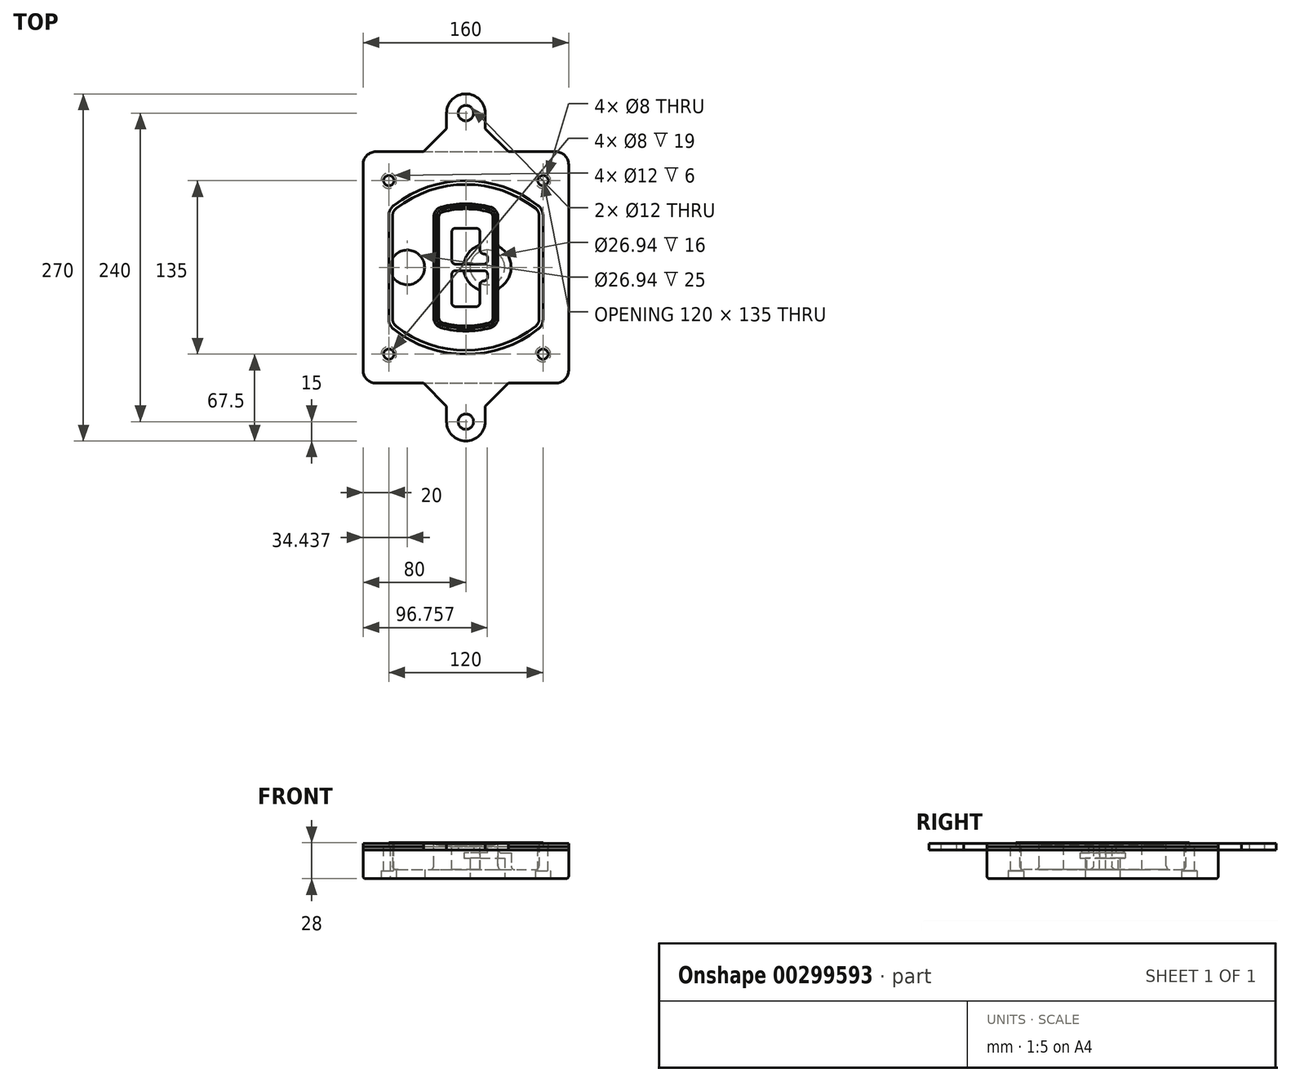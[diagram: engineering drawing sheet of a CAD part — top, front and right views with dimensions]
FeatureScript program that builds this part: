
annotation { "Feature Type Name" : "Feature", "Feature Type Description" : "" }
export const myFeature = defineFeature(function(context is Context, id is Id, definition is map)
    precondition{}
    {
        {
            var Q0;
            Q0=qCreatedBy(makeId("Top.planeOp"),FACE);
            var sketch = newSketch(context, id + "F0", { "sketchPlane" : qUnion([Q0])});
            skPoint(sketch, "E0.rect.middle", {"position": v(0, 0) * mm});
            skLineSegment(sketch, "E1.bottom", {"start": v(-70, -90) * mm, "end": v(70, -90) * mm});
            skLineSegment(sketch, "E1.top", {"start": v(-70, 90) * mm, "end": v(70, 90) * mm});
            skLineSegment(sketch, "E1.left", {"start": v(-80, -80) * mm, "end": v(-80, 80) * mm});
            skLineSegment(sketch, "E1.right", {"start": v(80, -80) * mm, "end": v(80, 80) * mm});
            skLineSegment(sketch, "E2", {"start": v(-80, 90) * mm, "end": v(80, -90) * mm, "construction": true});
            skLineSegment(sketch, "E3", {"start": v(80, 90) * mm, "end": v(-80, -90) * mm, "construction": true});
            skCircle(sketch, "E4", {"center": v(-60, 67.5) * mm, "radius": 4 * mm});
            skCircle(sketch, "E5", {"center": v(60, 67.5) * mm, "radius": 4 * mm});
            skCircle(sketch, "E6", {"center": v(60, -67.5) * mm, "radius": 4 * mm});
            skCircle(sketch, "E7", {"center": v(-60, -67.5) * mm, "radius": 4 * mm});
            skLineSegment(sketch, "E8", {"start": v(-60, 67.5) * mm, "end": v(60, 67.5) * mm, "construction": true});
            skLineSegment(sketch, "E9", {"start": v(60, 67.5) * mm, "end": v(60, -67.5) * mm, "construction": true});
            skLineSegment(sketch, "E10", {"start": v(60, -67.5) * mm, "end": v(-60, -67.5) * mm, "construction": true});
            skLineSegment(sketch, "E11", {"start": v(-60, -67.5) * mm, "end": v(-60, 67.5) * mm, "construction": true});
            skLineSegment(sketch, "E12", {"start": v(-60, 40.3) * mm, "end": v(-60, -40.3) * mm});
            skLineSegment(sketch, "E13", {"start": v(60, 40.3) * mm, "end": v(60, -40.3) * mm});
            skArc(sketch, "E14", {"start": v(56.15, 48.18) * mm, "mid": v(0, 67.5) * mm, "end": v(-56.15, 48.18) * mm});
            skArc(sketch, "E15", {"start": v(-56.15, -48.18) * mm, "mid": v(0, -67.5) * mm, "end": v(56.15, -48.18) * mm});
            skLineSegment(sketch, "E16", {"start": v(-60, 0) * mm, "end": v(60, 0) * mm, "construction": true});
            skPoint(sketch, "E17.visualSharp", {"position": v(-60, -45) * mm});
            skArc(sketch, "E17.filletArc", {"start": v(-60, -40.3) * mm, "mid": v(-58.99, -44.68) * mm, "end": v(-56.15, -48.18) * mm});
            skPoint(sketch, "E18.visualSharp", {"position": v(-60, 45) * mm});
            skArc(sketch, "E18.filletArc", {"start": v(-56.15, 48.18) * mm, "mid": v(-58.99, 44.68) * mm, "end": v(-60, 40.3) * mm});
            skPoint(sketch, "E19.visualSharp", {"position": v(60, 45) * mm});
            skArc(sketch, "E19.filletArc", {"start": v(60, 40.3) * mm, "mid": v(58.99, 44.68) * mm, "end": v(56.15, 48.18) * mm});
            skPoint(sketch, "E20.visualSharp", {"position": v(60, -45) * mm});
            skArc(sketch, "E20.filletArc", {"start": v(56.15, -48.18) * mm, "mid": v(58.99, -44.68) * mm, "end": v(60, -40.3) * mm});
            skPoint(sketch, "E21.visualSharp", {"position": v(-80, 90) * mm});
            skArc(sketch, "E21.filletArc", {"start": v(-70, 90) * mm, "mid": v(-77.07, 87.07) * mm, "end": v(-80, 80) * mm});
            skPoint(sketch, "E22.visualSharp", {"position": v(80, 90) * mm});
            skArc(sketch, "E22.filletArc", {"start": v(80, 80) * mm, "mid": v(77.07, 87.07) * mm, "end": v(70, 90) * mm});
            skPoint(sketch, "E23.visualSharp", {"position": v(80, -90) * mm});
            skArc(sketch, "E23.filletArc", {"start": v(70, -90) * mm, "mid": v(77.07, -87.07) * mm, "end": v(80, -80) * mm});
            skPoint(sketch, "E24.visualSharp", {"position": v(-80, -90) * mm});
            skArc(sketch, "E24.filletArc", {"start": v(-80, -80) * mm, "mid": v(-77.07, -87.07) * mm, "end": v(-70, -90) * mm});
            skArc(sketch, "E25.0", {"start": v(57, 40.3) * mm, "mid": v(56.3, 43.36) * mm, "end": v(54.3, 45.81) * mm});
            skLineSegment(sketch, "E25.1", {"start": v(57, 40.3) * mm, "end": v(57, -40.3) * mm});
            skArc(sketch, "E25.2", {"start": v(54.3, -45.81) * mm, "mid": v(56.3, -43.36) * mm, "end": v(57, -40.3) * mm});
            skArc(sketch, "E25.3", {"start": v(-54.3, -45.81) * mm, "mid": v(0, -64.5) * mm, "end": v(54.3, -45.81) * mm});
            skArc(sketch, "E25.4", {"start": v(-57, -40.3) * mm, "mid": v(-56.3, -43.36) * mm, "end": v(-54.3, -45.81) * mm});
            skArc(sketch, "E25.5", {"start": v(54.3, 45.81) * mm, "mid": v(0, 64.5) * mm, "end": v(-54.3, 45.81) * mm});
            skLineSegment(sketch, "E25.6", {"start": v(-57, 40.3) * mm, "end": v(-57, -40.3) * mm});
            skArc(sketch, "E25.7", {"start": v(-54.3, 45.81) * mm, "mid": v(-56.3, 43.36) * mm, "end": v(-57, 40.3) * mm});
            skArc(sketch, "E26.0", {"start": v(-58.62, 51.33) * mm, "mid": v(-62.58, 46.43) * mm, "end": v(-64, 40.3) * mm});
            skArc(sketch, "E26.1", {"start": v(58.62, 51.33) * mm, "mid": v(0, 71.5) * mm, "end": v(-58.62, 51.33) * mm});
            skArc(sketch, "E26.2", {"start": v(64, 40.3) * mm, "mid": v(62.58, 46.43) * mm, "end": v(58.62, 51.33) * mm});
            skLineSegment(sketch, "E26.3", {"start": v(64, 40.3) * mm, "end": v(64, -40.3) * mm});
            skArc(sketch, "E26.4", {"start": v(58.62, -51.33) * mm, "mid": v(62.58, -46.43) * mm, "end": v(64, -40.3) * mm});
            skLineSegment(sketch, "E26.5", {"start": v(-64, 40.3) * mm, "end": v(-64, -40.3) * mm});
            skArc(sketch, "E26.6", {"start": v(-58.62, -51.33) * mm, "mid": v(0, -71.5) * mm, "end": v(58.62, -51.33) * mm});
            skArc(sketch, "E26.7", {"start": v(-64, -40.3) * mm, "mid": v(-62.58, -46.43) * mm, "end": v(-58.62, -51.33) * mm});
            skSolve(sketch);
        }
        {
            var Q0;
            Q0=makeQuery(id+"F0.imprint","IMPRINT",FACE,{"disambiguationData":[TD([[makeQuery(id+"F0.imprint","IMPRINT",EDGE,{"derivedFrom":sQuery(id+"F0.wireOp",EDGE,"E1.bottom")}),1.0]])]});
            var Q1;
            Q1=makeQuery(id+"F0.imprint","IMPRINT",FACE,{"disambiguationData":[TD([[makeQuery(id+"F0.imprint","IMPRINT",EDGE,{"derivedFrom":sQuery(id+"F0.wireOp",EDGE,"E12")}),1.0]])]});
            var Q2;
            Q2=makeQuery(id+"F0.imprint","IMPRINT",FACE,{"disambiguationData":[TD([[makeQuery(id+"F0.imprint","IMPRINT",EDGE,{"derivedFrom":sQuery(id+"F0.wireOp",EDGE,"E25.0")}),1.0]])]});
            var Q3;
            Q3=makeQuery(id+"F0.imprint","IMPRINT",FACE,{"disambiguationData":[TD([[makeQuery(id+"F0.imprint","IMPRINT",EDGE,{"derivedFrom":sQuery(id+"F0.wireOp",EDGE,"E12")}),-1.0]])]});
            extrude(context, id + "F1", {"entities" : qUnion([Q0, Q1, Q2, Q3]), "oppositeDirection" : true, "depth" : 25 * mm});
        }
        {
            var Q0;
            Q0=makeQuery(id+"F0.imprint","IMPRINT",FACE,{"disambiguationData":[TD([[makeQuery(id+"F0.imprint","IMPRINT",EDGE,{"derivedFrom":sQuery(id+"F0.wireOp",EDGE,"E12")}),1.0]])]});
            extrude(context, id + "F2", {"entities" : qUnion([Q0]), "operationType" : NewBodyOperationType.ADD, "depth" : 3 * mm});
        }
        {
            var Q0;
            Q0=makeQuery(id+"F0.imprint","IMPRINT",FACE,{"disambiguationData":[TD([[makeQuery(id+"F0.imprint","IMPRINT",EDGE,{"derivedFrom":sQuery(id+"F0.wireOp",EDGE,"E25.0")}),1.0]])]});
            extrude(context, id + "F3", {"entities" : qUnion([Q0]), "operationType" : NewBodyOperationType.REMOVE, "oppositeDirection" : true, "depth" : 18 * mm});
        }
        {
            var Q0;
            Q0=makeQuery(id+"F2.opExtrude","CAP_FACE",FACE,{"disambiguationData":[OSD([sQuery(id+"F0.wireOp",EDGE,"E12"),sQuery(id+"F0.wireOp",EDGE,"E13"),sQuery(id+"F0.wireOp",EDGE,"E14"),sQuery(id+"F0.wireOp",EDGE,"E15"),sQuery(id+"F0.wireOp",EDGE,"E17.filletArc"),sQuery(id+"F0.wireOp",EDGE,"E18.filletArc"),sQuery(id+"F0.wireOp",EDGE,"E19.filletArc"),sQuery(id+"F0.wireOp",EDGE,"E20.filletArc"),sQuery(id+"F0.wireOp",EDGE,"E25.0"),sQuery(id+"F0.wireOp",EDGE,"E25.1"),sQuery(id+"F0.wireOp",EDGE,"E25.2"),sQuery(id+"F0.wireOp",EDGE,"E25.3"),sQuery(id+"F0.wireOp",EDGE,"E25.4"),sQuery(id+"F0.wireOp",EDGE,"E25.5"),sQuery(id+"F0.wireOp",EDGE,"E25.6"),sQuery(id+"F0.wireOp",EDGE,"E25.7")])],"isStart":false});
            var sketch = newSketch(context, id + "F4", { "sketchPlane" : qUnion([Q0])});
            skArc(sketch, "E27.0", {"start": v(-19.08, -46.97) * mm, "mid": v(0, -49.5) * mm, "end": v(19.08, -46.97) * mm});
            skArc(sketch, "E28.0", {"start": v(19.08, 46.97) * mm, "mid": v(0, 49.5) * mm, "end": v(-19.08, 46.97) * mm});
            skLineSegment(sketch, "E29", {"start": v(-25, 39.25) * mm, "end": v(-25, -39.25) * mm});
            skLineSegment(sketch, "E30", {"start": v(25, 39.25) * mm, "end": v(25, -39.25) * mm});
            skLineSegment(sketch, "E31", {"start": v(-25, 45.1) * mm, "end": v(25, 45.1) * mm, "construction": true});
            skLineSegment(sketch, "E32", {"start": v(-25, -45.1) * mm, "end": v(25, -45.1) * mm, "construction": true});
            skPoint(sketch, "E33.visualSharp", {"position": v(-25, 45.1) * mm});
            skArc(sketch, "E33.filletArc", {"start": v(-19.08, 46.97) * mm, "mid": v(-23.35, 44.11) * mm, "end": v(-25, 39.25) * mm});
            skPoint(sketch, "E34.visualSharp", {"position": v(25, 45.1) * mm});
            skArc(sketch, "E34.filletArc", {"start": v(25, 39.25) * mm, "mid": v(23.35, 44.11) * mm, "end": v(19.08, 46.97) * mm});
            skPoint(sketch, "E35.visualSharp", {"position": v(25, -45.1) * mm});
            skArc(sketch, "E35.filletArc", {"start": v(19.08, -46.97) * mm, "mid": v(23.35, -44.11) * mm, "end": v(25, -39.25) * mm});
            skPoint(sketch, "E36.visualSharp", {"position": v(-25, -45.1) * mm});
            skArc(sketch, "E36.filletArc", {"start": v(-25, -39.25) * mm, "mid": v(-23.35, -44.11) * mm, "end": v(-19.08, -46.97) * mm});
            skArc(sketch, "E37.0", {"start": v(54.3, 45.81) * mm, "mid": v(0, 64.5) * mm, "end": v(-54.3, 45.81) * mm});
            skArc(sketch, "E37.1", {"start": v(-54.3, 45.81) * mm, "mid": v(-56.3, 43.36) * mm, "end": v(-57, 40.3) * mm});
            skLineSegment(sketch, "E37.2", {"start": v(-57, 40.3) * mm, "end": v(-57, -40.3) * mm});
            skArc(sketch, "E37.3", {"start": v(-57, -40.3) * mm, "mid": v(-56.3, -43.36) * mm, "end": v(-54.3, -45.81) * mm});
            skArc(sketch, "E37.4", {"start": v(-54.3, -45.81) * mm, "mid": v(0, -64.5) * mm, "end": v(54.3, -45.81) * mm});
            skArc(sketch, "E37.5", {"start": v(54.3, -45.81) * mm, "mid": v(56.3, -43.36) * mm, "end": v(57, -40.3) * mm});
            skLineSegment(sketch, "E37.6", {"start": v(57, 40.3) * mm, "end": v(57, -40.3) * mm});
            skArc(sketch, "E37.7", {"start": v(57, 40.3) * mm, "mid": v(56.3, 43.36) * mm, "end": v(54.3, 45.81) * mm});
            skLineSegment(sketch, "E38.0", {"start": v(23, 39.25) * mm, "end": v(23, -39.25) * mm});
            skArc(sketch, "E38.1", {"start": v(18.56, -45.04) * mm, "mid": v(21.76, -42.9) * mm, "end": v(23, -39.25) * mm});
            skArc(sketch, "E38.2", {"start": v(-18.56, -45.04) * mm, "mid": v(0, -47.5) * mm, "end": v(18.56, -45.04) * mm});
            skArc(sketch, "E38.3", {"start": v(-23, -39.25) * mm, "mid": v(-21.76, -42.9) * mm, "end": v(-18.56, -45.04) * mm});
            skLineSegment(sketch, "E38.4", {"start": v(-23, 39.25) * mm, "end": v(-23, -39.25) * mm});
            skArc(sketch, "E38.5", {"start": v(23, 39.25) * mm, "mid": v(21.76, 42.9) * mm, "end": v(18.56, 45.04) * mm});
            skArc(sketch, "E38.6", {"start": v(-18.56, 45.04) * mm, "mid": v(-21.76, 42.9) * mm, "end": v(-23, 39.25) * mm});
            skArc(sketch, "E38.7", {"start": v(18.56, 45.04) * mm, "mid": v(0, 47.5) * mm, "end": v(-18.56, 45.04) * mm});
            skArc(sketch, "E39.0", {"start": v(21, 39.25) * mm, "mid": v(20.18, 41.68) * mm, "end": v(18.04, 43.1) * mm});
            skLineSegment(sketch, "E39.1", {"start": v(21, 39.25) * mm, "end": v(21, -39.25) * mm});
            skArc(sketch, "E39.2", {"start": v(18.04, -43.1) * mm, "mid": v(20.18, -41.68) * mm, "end": v(21, -39.25) * mm});
            skArc(sketch, "E39.3", {"start": v(-18.04, -43.1) * mm, "mid": v(0, -45.5) * mm, "end": v(18.04, -43.1) * mm});
            skArc(sketch, "E39.4", {"start": v(-21, -39.25) * mm, "mid": v(-20.18, -41.68) * mm, "end": v(-18.04, -43.1) * mm});
            skArc(sketch, "E39.5", {"start": v(18.04, 43.1) * mm, "mid": v(0, 45.5) * mm, "end": v(-18.04, 43.1) * mm});
            skLineSegment(sketch, "E39.6", {"start": v(-21, 39.25) * mm, "end": v(-21, -39.25) * mm});
            skArc(sketch, "E39.7", {"start": v(-18.04, 43.1) * mm, "mid": v(-20.18, 41.68) * mm, "end": v(-21, 39.25) * mm});
            skLineSegment(sketch, "E40", {"start": v(-25, 0) * mm, "end": v(25, 0) * mm, "construction": true});
            skLineSegment(sketch, "E41", {"start": v(-11, 5.5) * mm, "end": v(-11, 27.5) * mm});
            skLineSegment(sketch, "E42", {"start": v(-8, 30.5) * mm, "end": v(8, 30.5) * mm});
            skLineSegment(sketch, "E43", {"start": v(11, 27.5) * mm, "end": v(11, 13.5) * mm});
            skLineSegment(sketch, "E44", {"start": v(14, 10.5) * mm, "end": v(14, 10.5) * mm});
            skLineSegment(sketch, "E45", {"start": v(17, 7.5) * mm, "end": v(17, 5.5) * mm});
            skLineSegment(sketch, "E46", {"start": v(14, 2.5) * mm, "end": v(-8, 2.5) * mm});
            skPoint(sketch, "E47.visualSharp", {"position": v(-11, 30.5) * mm});
            skArc(sketch, "E47.filletArc", {"start": v(-8, 30.5) * mm, "mid": v(-10.12, 29.62) * mm, "end": v(-11, 27.5) * mm});
            skPoint(sketch, "E48.visualSharp", {"position": v(11, 30.5) * mm});
            skArc(sketch, "E48.filletArc", {"start": v(11, 27.5) * mm, "mid": v(10.12, 29.62) * mm, "end": v(8, 30.5) * mm});
            skPoint(sketch, "E49.visualSharp", {"position": v(11, 10.5) * mm});
            skArc(sketch, "E49.filletArc", {"start": v(11, 13.5) * mm, "mid": v(11.88, 11.38) * mm, "end": v(14, 10.5) * mm});
            skPoint(sketch, "E50.visualSharp", {"position": v(17, 10.5) * mm});
            skArc(sketch, "E50.filletArc", {"start": v(17, 7.5) * mm, "mid": v(16.12, 9.62) * mm, "end": v(14, 10.5) * mm});
            skPoint(sketch, "E51.visualSharp", {"position": v(17, 2.5) * mm});
            skArc(sketch, "E51.filletArc", {"start": v(14, 2.5) * mm, "mid": v(16.12, 3.38) * mm, "end": v(17, 5.5) * mm});
            skPoint(sketch, "E52.visualSharp", {"position": v(-11, 2.5) * mm});
            skArc(sketch, "E52.filletArc", {"start": v(-11, 5.5) * mm, "mid": v(-10.12, 3.38) * mm, "end": v(-8, 2.5) * mm});
            skLineSegment(sketch, "E53.0.MirrorCS", {"start": v(14, -2.5) * mm, "end": v(-8, -2.5) * mm});
            skArc(sketch, "E54.0.MirrorCS", {"start": v(-11, -5.5) * mm, "mid": v(-10.12, -3.38) * mm, "end": v(-8, -2.5) * mm});
            skLineSegment(sketch, "E55.0.MirrorCS", {"start": v(-11, -5.5) * mm, "end": v(-11, -27.5) * mm});
            skArc(sketch, "E56.0.MirrorCS", {"start": v(-8, -30.5) * mm, "mid": v(-10.12, -29.62) * mm, "end": v(-11, -27.5) * mm});
            skLineSegment(sketch, "E57.0.MirrorCS", {"start": v(-8, -30.5) * mm, "end": v(8, -30.5) * mm});
            skArc(sketch, "E58.0.MirrorCS", {"start": v(11, -27.5) * mm, "mid": v(10.12, -29.62) * mm, "end": v(8, -30.5) * mm});
            skLineSegment(sketch, "E59.0.MirrorCS", {"start": v(11, -27.5) * mm, "end": v(11, -13.5) * mm});
            skArc(sketch, "E60.0.MirrorCS", {"start": v(11, -13.5) * mm, "mid": v(11.88, -11.38) * mm, "end": v(14, -10.5) * mm});
            skArc(sketch, "E61.0.MirrorCS", {"start": v(17, -7.5) * mm, "mid": v(16.12, -9.62) * mm, "end": v(14, -10.5) * mm});
            skLineSegment(sketch, "E62.0.MirrorCS", {"start": v(17, -7.5) * mm, "end": v(17, -5.5) * mm});
            skArc(sketch, "E63.0.MirrorCS", {"start": v(14, -2.5) * mm, "mid": v(16.12, -3.38) * mm, "end": v(17, -5.5) * mm});
            skSolve(sketch);
        }
        {
            var Q0;
            Q0=makeQuery(id+"F4.imprint","IMPRINT",FACE,{"disambiguationData":[TD([[makeQuery(id+"F4.imprint","IMPRINT",EDGE,{"derivedFrom":sQuery(id+"F4.wireOp",EDGE,"E27.0")}),1.0]])]});
            var Q1;
            Q1=makeQuery(id+"F4.imprint","IMPRINT",FACE,{"disambiguationData":[TD([[makeQuery(id+"F4.imprint","IMPRINT",EDGE,{"derivedFrom":sQuery(id+"F4.wireOp",EDGE,"E38.0")}),-1.0]])]});
            var Q2;
            Q2=makeQuery(id+"F4.imprint","IMPRINT",FACE,{"disambiguationData":[TD([[makeQuery(id+"F4.imprint","IMPRINT",EDGE,{"derivedFrom":sQuery(id+"F4.wireOp",EDGE,"E39.0")}),1.0]])]});
            extrude(context, id + "F5", {"entities" : qUnion([Q0, Q1, Q2]), "operationType" : NewBodyOperationType.ADD, "endBound" : BoundingType.UP_TO_NEXT, "oppositeDirection" : true, "depth" : 25 * mm});
        }
        {
            var Q0;
            Q0=makeQuery(id+"F4.imprint","IMPRINT",FACE,{"disambiguationData":[TD([[makeQuery(id+"F4.imprint","IMPRINT",EDGE,{"derivedFrom":sQuery(id+"F4.wireOp",EDGE,"E38.0")}),-1.0]])]});
            extrude(context, id + "F6", {"entities" : qUnion([Q0]), "operationType" : NewBodyOperationType.REMOVE, "oppositeDirection" : true, "depth" : 2 * mm});
        }
        {
            var Q0;
            Q0=makeQuery(id+"F1.opExtrude","CAP_FACE",FACE,{"disambiguationData":[OSD([sQuery(id+"F0.wireOp",EDGE,"E1.bottom"),sQuery(id+"F0.wireOp",EDGE,"E1.top"),sQuery(id+"F0.wireOp",EDGE,"E1.left"),sQuery(id+"F0.wireOp",EDGE,"E1.right"),sQuery(id+"F0.wireOp",EDGE,"E4"),sQuery(id+"F0.wireOp",EDGE,"E5"),sQuery(id+"F0.wireOp",EDGE,"E6"),sQuery(id+"F0.wireOp",EDGE,"E7"),sQuery(id+"F0.wireOp",EDGE,"E21.filletArc"),sQuery(id+"F0.wireOp",EDGE,"E22.filletArc"),sQuery(id+"F0.wireOp",EDGE,"E23.filletArc"),sQuery(id+"F0.wireOp",EDGE,"E24.filletArc")])],"isStart":false});
            var sketch = newSketch(context, id + "F7", { "sketchPlane" : qUnion([Q0])});
            skCircle(sketch, "E64", {"center": v(16.76, 0) * mm, "radius": 13.47 * mm});
            skCircle(sketch, "E65", {"center": v(-45.56, 0) * mm, "radius": 13.47 * mm});
            skLineSegment(sketch, "E66", {"start": v(80, 0) * mm, "end": v(-80, 0) * mm});
            skCircle(sketch, "E67", {"center": v(16.76, 0) * mm, "radius": 18.47 * mm});
            skCircle(sketch, "E68", {"center": v(60, -67.5) * mm, "radius": 6 * mm});
            skCircle(sketch, "E69", {"center": v(-60, -67.5) * mm, "radius": 6 * mm});
            skCircle(sketch, "E70", {"center": v(-60, 67.5) * mm, "radius": 6 * mm});
            skCircle(sketch, "E71", {"center": v(60, 67.5) * mm, "radius": 6 * mm});
            skSolve(sketch);
        }
        {
            var Q0;
            {var subQ1=sQuery(id+"F7.wireOp",EDGE,"E66");var subQ4=sQuery(id+"F7.wireOp",EDGE,"E64");var subQ6=makeQuery(id+"F7.imprint","INTERSECT",VERTEX,{"disambiguationData":[OD(0.0)],"derivedFrom":[subQ4,subQ1]});Q0=makeQuery(id+"F7.imprint","IMPRINT",FACE,{"disambiguationData":[TD([[makeQuery(id+"F7.imprint","IMPRINT",EDGE,{"disambiguationData":[TD([[subQ6,-1.0]])],"derivedFrom":subQ4}),-1.0]])]});}
            var Q1;
            {var subQ0=sQuery(id+"F7.wireOp",EDGE,"E66");var subQ1=sQuery(id+"F7.wireOp",EDGE,"E64");var subQ3=makeQuery(id+"F7.imprint","INTERSECT",VERTEX,{"disambiguationData":[OD(0.0)],"derivedFrom":[subQ1,subQ0]});Q1=makeQuery(id+"F7.imprint","IMPRINT",FACE,{"disambiguationData":[TD([[makeQuery(id+"F7.imprint","IMPRINT",EDGE,{"disambiguationData":[TD([[subQ3,-1.0]])],"derivedFrom":subQ1}),1.0]])]});}
            var Q2;
            {var subQ0=sQuery(id+"F7.wireOp",EDGE,"E66");var subQ1=sQuery(id+"F7.wireOp",EDGE,"E64");var subQ3=makeQuery(id+"F7.imprint","INTERSECT",VERTEX,{"disambiguationData":[OD(0.0)],"derivedFrom":[subQ1,subQ0]});Q2=makeQuery(id+"F7.imprint","IMPRINT",FACE,{"disambiguationData":[TD([[makeQuery(id+"F7.imprint","IMPRINT",EDGE,{"disambiguationData":[TD([[subQ3,1.0]])],"derivedFrom":subQ1}),1.0]])]});}
            var Q3;
            {var subQ1=sQuery(id+"F7.wireOp",EDGE,"E66");var subQ4=sQuery(id+"F7.wireOp",EDGE,"E64");var subQ6=makeQuery(id+"F7.imprint","INTERSECT",VERTEX,{"disambiguationData":[OD(0.0)],"derivedFrom":[subQ4,subQ1]});Q3=makeQuery(id+"F7.imprint","IMPRINT",FACE,{"disambiguationData":[TD([[makeQuery(id+"F7.imprint","IMPRINT",EDGE,{"disambiguationData":[TD([[subQ6,1.0]])],"derivedFrom":subQ4}),-1.0]])]});}
            extrude(context, id + "F8", {"entities" : qUnion([Q0, Q1, Q2, Q3]), "operationType" : NewBodyOperationType.ADD, "oppositeDirection" : true, "depth" : 20 * mm});
        }
        {
            var Q0;
            {var subQ0=sQuery(id+"F7.wireOp",EDGE,"E66");var subQ1=sQuery(id+"F7.wireOp",EDGE,"E64");var subQ3=makeQuery(id+"F7.imprint","INTERSECT",VERTEX,{"disambiguationData":[OD(0.0)],"derivedFrom":[subQ1,subQ0]});Q0=makeQuery(id+"F7.imprint","IMPRINT",FACE,{"disambiguationData":[TD([[makeQuery(id+"F7.imprint","IMPRINT",EDGE,{"disambiguationData":[TD([[subQ3,-1.0]])],"derivedFrom":subQ1}),1.0]])]});}
            var Q1;
            {var subQ0=sQuery(id+"F7.wireOp",EDGE,"E66");var subQ1=sQuery(id+"F7.wireOp",EDGE,"E64");var subQ3=makeQuery(id+"F7.imprint","INTERSECT",VERTEX,{"disambiguationData":[OD(0.0)],"derivedFrom":[subQ1,subQ0]});Q1=makeQuery(id+"F7.imprint","IMPRINT",FACE,{"disambiguationData":[TD([[makeQuery(id+"F7.imprint","IMPRINT",EDGE,{"disambiguationData":[TD([[subQ3,1.0]])],"derivedFrom":subQ1}),1.0]])]});}
            extrude(context, id + "F9", {"entities" : qUnion([Q0, Q1]), "operationType" : NewBodyOperationType.REMOVE, "oppositeDirection" : true, "depth" : 16 * mm});
        }
        {
            var Q0;
            {var subQ0=sQuery(id+"F7.wireOp",EDGE,"E66");var subQ1=sQuery(id+"F7.wireOp",EDGE,"E65");var subQ3=makeQuery(id+"F7.imprint","INTERSECT",VERTEX,{"disambiguationData":[OD(0.0)],"derivedFrom":[subQ1,subQ0]});Q0=makeQuery(id+"F7.imprint","IMPRINT",FACE,{"disambiguationData":[TD([[makeQuery(id+"F7.imprint","IMPRINT",EDGE,{"disambiguationData":[TD([[subQ3,-1.0]])],"derivedFrom":subQ1}),1.0]])]});}
            var Q1;
            {var subQ0=sQuery(id+"F7.wireOp",EDGE,"E66");var subQ1=sQuery(id+"F7.wireOp",EDGE,"E65");var subQ3=makeQuery(id+"F7.imprint","INTERSECT",VERTEX,{"disambiguationData":[OD(0.0)],"derivedFrom":[subQ1,subQ0]});Q1=makeQuery(id+"F7.imprint","IMPRINT",FACE,{"disambiguationData":[TD([[makeQuery(id+"F7.imprint","IMPRINT",EDGE,{"disambiguationData":[TD([[subQ3,1.0]])],"derivedFrom":subQ1}),1.0]])]});}
            extrude(context, id + "F10", {"entities" : qUnion([Q0, Q1]), "operationType" : NewBodyOperationType.REMOVE, "oppositeDirection" : true, "depth" : 25 * mm});
        }
        {
            var Q0;
            Q0=makeQuery(id+"F7.imprint","IMPRINT",FACE,{"disambiguationData":[TD([[makeQuery(id+"F7.imprint","IMPRINT",EDGE,{"derivedFrom":sQuery(id+"F7.wireOp",EDGE,"E68")}),1.0]])]});
            var Q1;
            Q1=makeQuery(id+"F7.imprint","IMPRINT",FACE,{"disambiguationData":[TD([[makeQuery(id+"F7.imprint","IMPRINT",EDGE,{"derivedFrom":makeQuery(id+"F1.opExtrude","CAP_EDGE",EDGE,{"disambiguationData":[OSD([sQuery(id+"F0.wireOp",EDGE,"E5")])],"isStart":false})}),-1.0]])]});
            var Q2;
            Q2=makeQuery(id+"F7.imprint","IMPRINT",FACE,{"disambiguationData":[TD([[makeQuery(id+"F7.imprint","IMPRINT",EDGE,{"derivedFrom":sQuery(id+"F7.wireOp",EDGE,"E69")}),1.0]])]});
            var Q3;
            Q3=makeQuery(id+"F7.imprint","IMPRINT",FACE,{"disambiguationData":[TD([[makeQuery(id+"F7.imprint","IMPRINT",EDGE,{"derivedFrom":makeQuery(id+"F1.opExtrude","CAP_EDGE",EDGE,{"disambiguationData":[OSD([sQuery(id+"F0.wireOp",EDGE,"E4")])],"isStart":false})}),-1.0]])]});
            var Q4;
            Q4=makeQuery(id+"F7.imprint","IMPRINT",FACE,{"disambiguationData":[TD([[makeQuery(id+"F7.imprint","IMPRINT",EDGE,{"derivedFrom":sQuery(id+"F7.wireOp",EDGE,"E70")}),1.0]])]});
            var Q5;
            Q5=makeQuery(id+"F7.imprint","IMPRINT",FACE,{"disambiguationData":[TD([[makeQuery(id+"F7.imprint","IMPRINT",EDGE,{"derivedFrom":makeQuery(id+"F1.opExtrude","CAP_EDGE",EDGE,{"disambiguationData":[OSD([sQuery(id+"F0.wireOp",EDGE,"E7")])],"isStart":false})}),-1.0]])]});
            var Q6;
            Q6=makeQuery(id+"F7.imprint","IMPRINT",FACE,{"disambiguationData":[TD([[makeQuery(id+"F7.imprint","IMPRINT",EDGE,{"derivedFrom":sQuery(id+"F7.wireOp",EDGE,"E71")}),1.0]])]});
            var Q7;
            Q7=makeQuery(id+"F7.imprint","IMPRINT",FACE,{"disambiguationData":[TD([[makeQuery(id+"F7.imprint","IMPRINT",EDGE,{"derivedFrom":makeQuery(id+"F1.opExtrude","CAP_EDGE",EDGE,{"disambiguationData":[OSD([sQuery(id+"F0.wireOp",EDGE,"E6")])],"isStart":false})}),-1.0]])]});
            extrude(context, id + "F11", {"entities" : qUnion([Q0, Q1, Q2, Q3, Q4, Q5, Q6, Q7]), "operationType" : NewBodyOperationType.REMOVE, "oppositeDirection" : true, "depth" : 6 * mm});
        }
        {
            var Q0;
            Q0=makeQuery(id+"F9.boolean.opBoolean","COPY",FACE,{"derivedFrom":makeQuery(id+"F9.opExtrude","CAP_FACE",FACE,{"disambiguationData":[OSD([sQuery(id+"F7.wireOp",EDGE,"E64")])],"isStart":false})});
            var sketch = newSketch(context, id + "F12", { "sketchPlane" : qUnion([Q0])});
            skArc(sketch, "E72.0", {"start": v(11, 17.55) * mm, "mid": v(2.57, 11.82) * mm, "end": v(-1.54, 2.5) * mm});
            skArc(sketch, "E72.1", {"start": v(-1.54, -2.5) * mm, "mid": v(2.57, -11.82) * mm, "end": v(11, -17.55) * mm});
            skLineSegment(sketch, "E73", {"start": v(-1.54, -2.5) * mm, "end": v(14, -2.5) * mm});
            skLineSegment(sketch, "E74.0", {"start": v(14, 2.5) * mm, "end": v(-1.54, 2.5) * mm});
            skArc(sketch, "E74.1", {"start": v(14, 2.5) * mm, "mid": v(16.12, 3.38) * mm, "end": v(17, 5.5) * mm});
            skLineSegment(sketch, "E74.2", {"start": v(17, 7.5) * mm, "end": v(17, 5.5) * mm});
            skArc(sketch, "E74.3", {"start": v(17, 7.5) * mm, "mid": v(16.12, 9.62) * mm, "end": v(14, 10.5) * mm});
            skArc(sketch, "E74.4", {"start": v(11, 13.5) * mm, "mid": v(11.88, 11.38) * mm, "end": v(14, 10.5) * mm});
            skLineSegment(sketch, "E74.5", {"start": v(11, 17.55) * mm, "end": v(11, 13.5) * mm});
            skLineSegment(sketch, "E74.7", {"start": v(14, -2.5) * mm, "end": v(-1.54, -2.5) * mm});
            skArc(sketch, "E74.8", {"start": v(14, -2.5) * mm, "mid": v(16.12, -3.38) * mm, "end": v(17, -5.5) * mm});
            skLineSegment(sketch, "E74.9", {"start": v(17, -7.5) * mm, "end": v(17, -5.5) * mm});
            skArc(sketch, "E74.10", {"start": v(17, -7.5) * mm, "mid": v(16.12, -9.62) * mm, "end": v(14, -10.5) * mm});
            skArc(sketch, "E74.11", {"start": v(11, -13.5) * mm, "mid": v(11.88, -11.38) * mm, "end": v(14, -10.5) * mm});
            skLineSegment(sketch, "E74.12", {"start": v(11, -17.55) * mm, "end": v(11, -13.5) * mm});
            skPoint(sketch, "E75.orphan", {"position": v(11, -27.5) * mm});
            skPoint(sketch, "E76.orphan", {"position": v(-8, -2.5) * mm});
            skPoint(sketch, "E77.orphan", {"position": v(-8, 2.5) * mm});
            skPoint(sketch, "E78.orphan", {"position": v(11, 27.5) * mm});
            skSolve(sketch);
        }
        {
            var Q0;
            {var subQ7=sQuery(id+"F12.wireOp",EDGE,"E72.0");var subQ14=sQuery(id+"F12.wireOp",EDGE,"E72.1");var subQ16=sQuery(id+"F12.wireOp",EDGE,"E74.1");var subQ18=sQuery(id+"F12.wireOp",EDGE,"E74.8");Q0=qUnion([makeQuery(id+"F12.imprint","IMPRINT",FACE,{"disambiguationData":[TD([[makeQuery(id+"F12.imprint","IMPRINT",EDGE,{"derivedFrom":subQ7}),1.0]])]}),makeQuery(id+"F12.imprint","IMPRINT",FACE,{"disambiguationData":[TD([[makeQuery(id+"F12.imprint","IMPRINT",EDGE,{"derivedFrom":subQ14}),1.0]])]}),makeQuery(id+"F12.imprint","IMPRINT",FACE,{"disambiguationData":[TD([[makeQuery(id+"F12.imprint","IMPRINT",EDGE,{"derivedFrom":subQ16}),1.0]])]}),makeQuery(id+"F12.imprint","IMPRINT",FACE,{"disambiguationData":[TD([[makeQuery(id+"F12.imprint","IMPRINT",EDGE,{"derivedFrom":subQ18}),-1.0]])]})]);}
            var Q1;
            Q1=makeQuery(id+"F5.boolean.opBoolean","SPLIT",FACE,{"disambiguationData":[TD([makeQuery(id+"F5.opExtrude","SWEPT_FACE",FACE,{"disambiguationData":[OSD([sQuery(id+"F4.wireOp",EDGE,"E41")])]})])],"derivedFrom":makeQuery(id+"F3.boolean.opBoolean","COPY",FACE,{"derivedFrom":makeQuery(id+"F3.opExtrude","CAP_FACE",FACE,{"disambiguationData":[OSD([sQuery(id+"F0.wireOp",EDGE,"E25.0"),sQuery(id+"F0.wireOp",EDGE,"E25.1"),sQuery(id+"F0.wireOp",EDGE,"E25.2"),sQuery(id+"F0.wireOp",EDGE,"E25.3"),sQuery(id+"F0.wireOp",EDGE,"E25.4"),sQuery(id+"F0.wireOp",EDGE,"E25.5"),sQuery(id+"F0.wireOp",EDGE,"E25.6"),sQuery(id+"F0.wireOp",EDGE,"E25.7")])],"isStart":false})})});
            extrude(context, id + "F13", {"entities" : qUnion([Q0]), "operationType" : NewBodyOperationType.REMOVE, "endBound" : BoundingType.UP_TO_SURFACE, "endBoundEntityFace" : qUnion([Q1]), "depth" : 25 * mm});
        }
        {
            var Q0;
            Q0=makeQuery(id+"F3.boolean.opBoolean","COPY",EDGE,{"derivedFrom":makeQuery(id+"F3.opExtrude","CAP_EDGE",EDGE,{"disambiguationData":[OSD([sQuery(id+"F0.wireOp",EDGE,"E25.6")])],"isStart":false})});
            var Q1;
            Q1=makeQuery(id+"F8.boolean.opBoolean","INTERSECT",EDGE,{"derivedFrom":[makeQuery(id+"F5.opExtrude","SWEPT_FACE",FACE,{"disambiguationData":[OSD([sQuery(id+"F4.wireOp",EDGE,"E30")])]}),makeQuery(id+"F8.opExtrude","CAP_FACE",FACE,{"disambiguationData":[OSD([sQuery(id+"F7.wireOp",EDGE,"E67")])],"isStart":false})]});
            var Q2;
            Q2=makeQuery(id+"F8.boolean.opBoolean","INTERSECT",EDGE,{"disambiguationData":[OD(1.0)],"derivedFrom":[makeQuery(id+"F5.opExtrude","SWEPT_FACE",FACE,{"disambiguationData":[OSD([sQuery(id+"F4.wireOp",EDGE,"E30")])]}),makeQuery(id+"F8.opExtrude","SWEPT_FACE",FACE,{"disambiguationData":[OSD([sQuery(id+"F7.wireOp",EDGE,"E67")])]})]});
            var Q3;
            {var subQ0=sQuery(id+"F4.wireOp",EDGE,"E30");Q3=makeQuery(id+"F8.boolean.opBoolean","SPLIT",EDGE,{"disambiguationData":[TD([makeQuery(id+"F5.opExtrude","SWEPT_FACE",FACE,{"disambiguationData":[OSD([sQuery(id+"F4.wireOp",EDGE,"E35.filletArc")])]})])],"derivedFrom":makeQuery(id+"F5.opExtrude","CAP_EDGE",EDGE,{"disambiguationData":[OSD([subQ0])],"isStart":false})});}
            var Q4;
            {var subQ0=sQuery(id+"F0.wireOp",EDGE,"E25.7");var subQ1=sQuery(id+"F0.wireOp",EDGE,"E25.1");var subQ2=sQuery(id+"F0.wireOp",EDGE,"E25.6");var subQ3=sQuery(id+"F0.wireOp",EDGE,"E25.5");var subQ4=sQuery(id+"F0.wireOp",EDGE,"E25.4");var subQ5=sQuery(id+"F0.wireOp",EDGE,"E25.0");var subQ6=sQuery(id+"F0.wireOp",EDGE,"E25.2");var subQ7=sQuery(id+"F0.wireOp",EDGE,"E25.3");Q4=makeQuery(id+"F8.boolean.opBoolean","INTERSECT",EDGE,{"derivedFrom":[makeQuery(id+"F5.boolean.opBoolean","SPLIT",FACE,{"disambiguationData":[TD([makeQuery(id+"F2.opExtrude","SWEPT_FACE",FACE,{"disambiguationData":[OSD([subQ5])]})])],"derivedFrom":makeQuery(id+"F3.boolean.opBoolean","COPY",FACE,{"derivedFrom":makeQuery(id+"F3.opExtrude","CAP_FACE",FACE,{"disambiguationData":[OSD([subQ5,subQ1,subQ6,subQ7,subQ4,subQ3,subQ2,subQ0])],"isStart":false})})}),makeQuery(id+"F8.opExtrude","SWEPT_FACE",FACE,{"disambiguationData":[OSD([sQuery(id+"F7.wireOp",EDGE,"E67")])]})]});}
            var Q5;
            Q5=makeQuery(id+"F8.boolean.opBoolean","INTERSECT",EDGE,{"disambiguationData":[OD(0.0)],"derivedFrom":[makeQuery(id+"F5.opExtrude","SWEPT_FACE",FACE,{"disambiguationData":[OSD([sQuery(id+"F4.wireOp",EDGE,"E30")])]}),makeQuery(id+"F8.opExtrude","SWEPT_FACE",FACE,{"disambiguationData":[OSD([sQuery(id+"F7.wireOp",EDGE,"E67")])]})]});
            fillet(context, id + "F14", {"entities" : qUnion([Q0, Q1, Q2, Q3, Q4, Q5]), "radius" : 3 * mm, "tangentPropagation" : true, "allowEdgeOverflow" : false});
        }
        {
            var Q0;
            Q0=makeQuery(id+"F1.opExtrude","CAP_EDGE",EDGE,{"disambiguationData":[OSD([sQuery(id+"F0.wireOp",EDGE,"E1.bottom")])],"isStart":false});
            fillet(context, id + "F15", {"entities" : qUnion([Q0]), "radius" : 2 * mm, "tangentPropagation" : true, "allowEdgeOverflow" : false});
        }
        {
            var Q0;
            {var subQ0=sQuery(id+"F0.wireOp",EDGE,"E21.filletArc");var subQ1=sQuery(id+"F0.wireOp",EDGE,"E7");var subQ2=sQuery(id+"F0.wireOp",EDGE,"E6");var subQ3=sQuery(id+"F0.wireOp",EDGE,"E5");var subQ4=sQuery(id+"F0.wireOp",EDGE,"E4");var subQ5=sQuery(id+"F0.wireOp",EDGE,"E22.filletArc");var subQ6=sQuery(id+"F0.wireOp",EDGE,"E1.bottom");var subQ7=sQuery(id+"F0.wireOp",EDGE,"E1.right");var subQ8=sQuery(id+"F0.wireOp",EDGE,"E1.top");var subQ9=sQuery(id+"F0.wireOp",EDGE,"E1.left");var subQ10=sQuery(id+"F0.wireOp",EDGE,"E23.filletArc");var subQ11=sQuery(id+"F0.wireOp",EDGE,"E24.filletArc");Q0=makeQuery(id+"F2.boolean.opBoolean","SPLIT",FACE,{"disambiguationData":[TD([makeQuery(id+"F1.opExtrude","SWEPT_FACE",FACE,{"disambiguationData":[OSD([subQ6])]})])],"derivedFrom":makeQuery(id+"F1.opExtrude","CAP_FACE",FACE,{"disambiguationData":[OSD([subQ6,subQ8,subQ9,subQ7,subQ4,subQ3,subQ2,subQ1,subQ0,subQ5,subQ10,subQ11])],"isStart":true})});}
            var sketch = newSketch(context, id + "F16", { "sketchPlane" : qUnion([Q0])});
            skLineSegment(sketch, "E79", {"start": v(0, 90) * mm, "end": v(0, 120) * mm, "construction": true});
            skCircle(sketch, "E80", {"center": v(0, 120) * mm, "radius": 6 * mm});
            skArc(sketch, "E81", {"start": v(15, 120) * mm, "mid": v(0, 135) * mm, "end": v(-15, 120) * mm});
            skLineSegment(sketch, "E82", {"start": v(-15, 120) * mm, "end": v(-15, 108) * mm});
            skLineSegment(sketch, "E83", {"start": v(15, 120) * mm, "end": v(15, 108) * mm});
            skLineSegment(sketch, "E84", {"start": v(15, 108) * mm, "end": v(33, 90) * mm});
            skLineSegment(sketch, "E85", {"start": v(-15, 108) * mm, "end": v(-33, 90) * mm});
            skLineSegment(sketch, "E86", {"start": v(-80, 0) * mm, "end": v(80, 0) * mm, "construction": true});
            skLineSegment(sketch, "E87.MirrorCS", {"start": v(15, -108) * mm, "end": v(33, -90) * mm});
            skLineSegment(sketch, "E88.MirrorCS", {"start": v(15, -120) * mm, "end": v(15, -108) * mm});
            skArc(sketch, "E89.MirrorCS", {"start": v(15, -120) * mm, "mid": v(0, -135) * mm, "end": v(-15, -120) * mm});
            skLineSegment(sketch, "E90.MirrorCS", {"start": v(-15, -120) * mm, "end": v(-15, -108) * mm});
            skLineSegment(sketch, "E91.MirrorCS", {"start": v(-15, -108) * mm, "end": v(-33, -90) * mm});
            skCircle(sketch, "E92.MirrorC", {"center": v(0, -120) * mm, "radius": 6 * mm});
            skLineSegment(sketch, "E93.MirrorCS", {"start": v(0, -90) * mm, "end": v(0, -120) * mm, "construction": true});
            skSolve(sketch);
        }
        {
            var Q0;
            Q0=makeQuery(id+"F16.imprint","IMPRINT",FACE,{"disambiguationData":[TD([[makeQuery(id+"F16.imprint","IMPRINT",EDGE,{"derivedFrom":sQuery(id+"F16.wireOp",EDGE,"E80")}),-1.0]])]});
            var Q1;
            Q1=makeQuery(id+"F16.imprint","IMPRINT",FACE,{"disambiguationData":[TD([[makeQuery(id+"F16.imprint","IMPRINT",EDGE,{"derivedFrom":makeQuery(id+"F1.opExtrude","CAP_EDGE",EDGE,{"disambiguationData":[OSD([sQuery(id+"F0.wireOp",EDGE,"E1.left")])],"isStart":true})}),-1.0]])]});
            var Q2;
            {var subQ0=sQuery(id+"F16.wireOp",EDGE,"E87.MirrorCS");Q2=makeQuery(id+"F16.imprint","IMPRINT",FACE,{"disambiguationData":[TD([[makeQuery(id+"F16.imprint","IMPRINT",EDGE,{"derivedFrom":subQ0}),1.0]])]});}
            extrude(context, id + "F17", {"entities" : qUnion([Q0, Q1, Q2]), "endBound" : BoundingType.SYMMETRIC, "depth" : 5 * mm});
        }
    });
